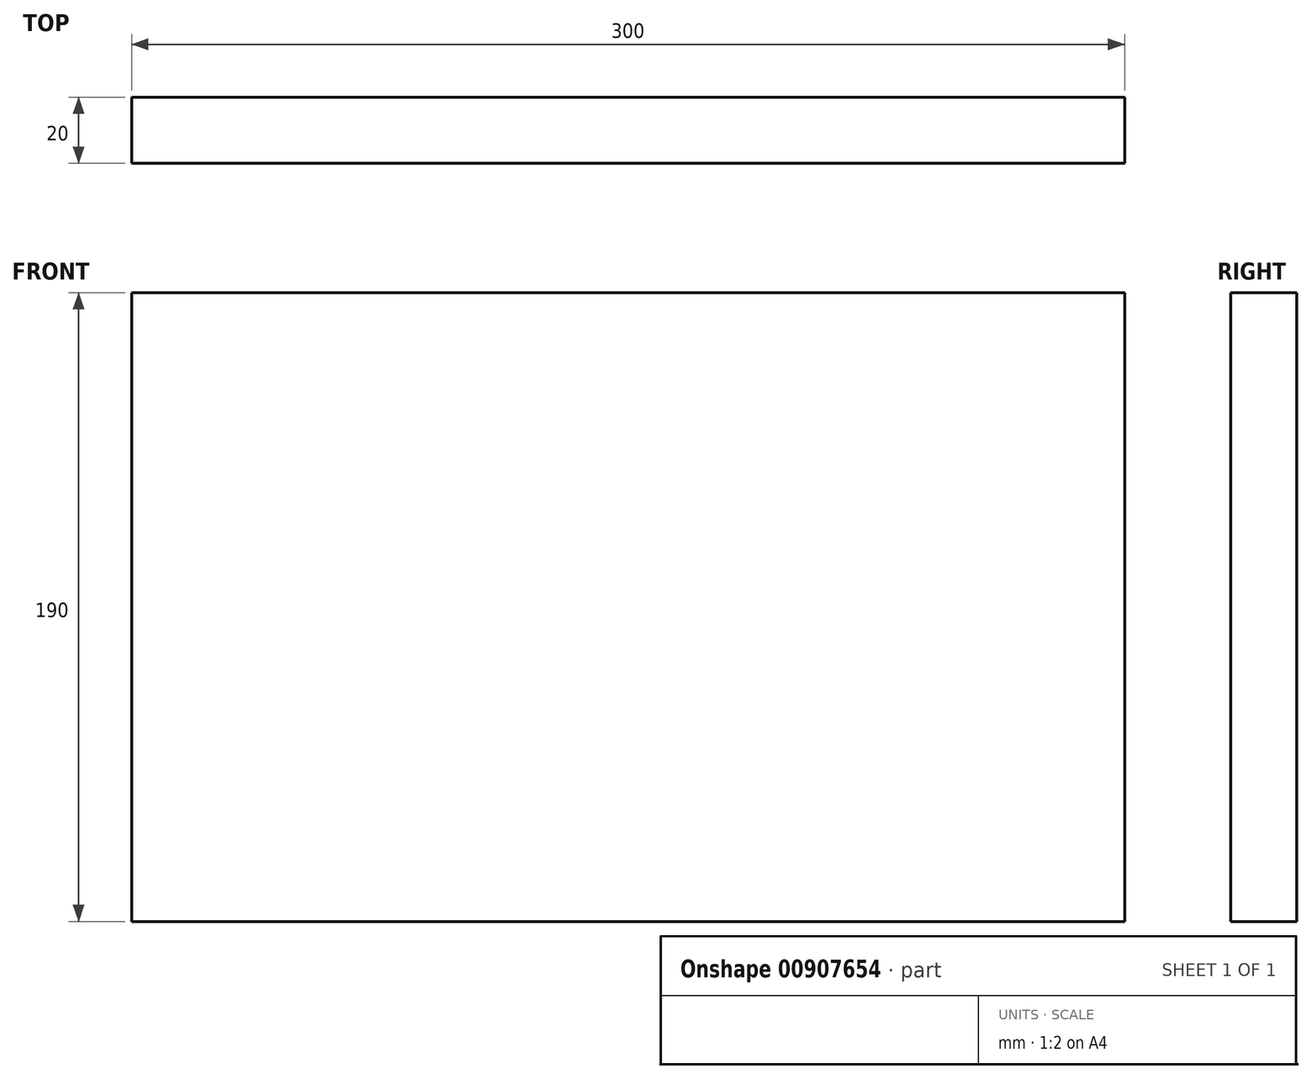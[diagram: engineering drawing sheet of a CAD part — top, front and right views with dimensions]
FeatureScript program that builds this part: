
annotation { "Feature Type Name" : "Feature", "Feature Type Description" : "" }
export const myFeature = defineFeature(function(context is Context, id is Id, definition is map)
    precondition{}
    {
        {
            var Q0;
            Q0=qCreatedBy(makeId("Front.planeOp"),FACE);
            var sketch = newSketch(context, id + "F0", { "sketchPlane" : qUnion([Q0])});
            skLineSegment(sketch, "E0.bottom", {"start": v(-203.5, -126.07) * mm, "end": v(96.5, -126.07) * mm});
            skLineSegment(sketch, "E0.top", {"start": v(-203.5, 63.93) * mm, "end": v(96.5, 63.93) * mm});
            skLineSegment(sketch, "E0.left", {"start": v(-203.5, -126.07) * mm, "end": v(-203.5, 63.93) * mm});
            skLineSegment(sketch, "E0.right", {"start": v(96.5, -126.07) * mm, "end": v(96.5, 63.93) * mm});
            skSolve(sketch);
        }
        {
            var Q0;
            Q0=makeQuery(id+"F0.imprint","IMPRINT",FACE,{"disambiguationData":[TD([[makeQuery(id+"F0.imprint","IMPRINT",EDGE,{"derivedFrom":sQuery(id+"F0.wireOp",EDGE,"E0.bottom")}),1.0]])]});
            extrude(context, id + "F1", {"entities" : qUnion([Q0]), "depth" : 20 * mm, "offsetDistance" : 25 * mm});
        }
    });
